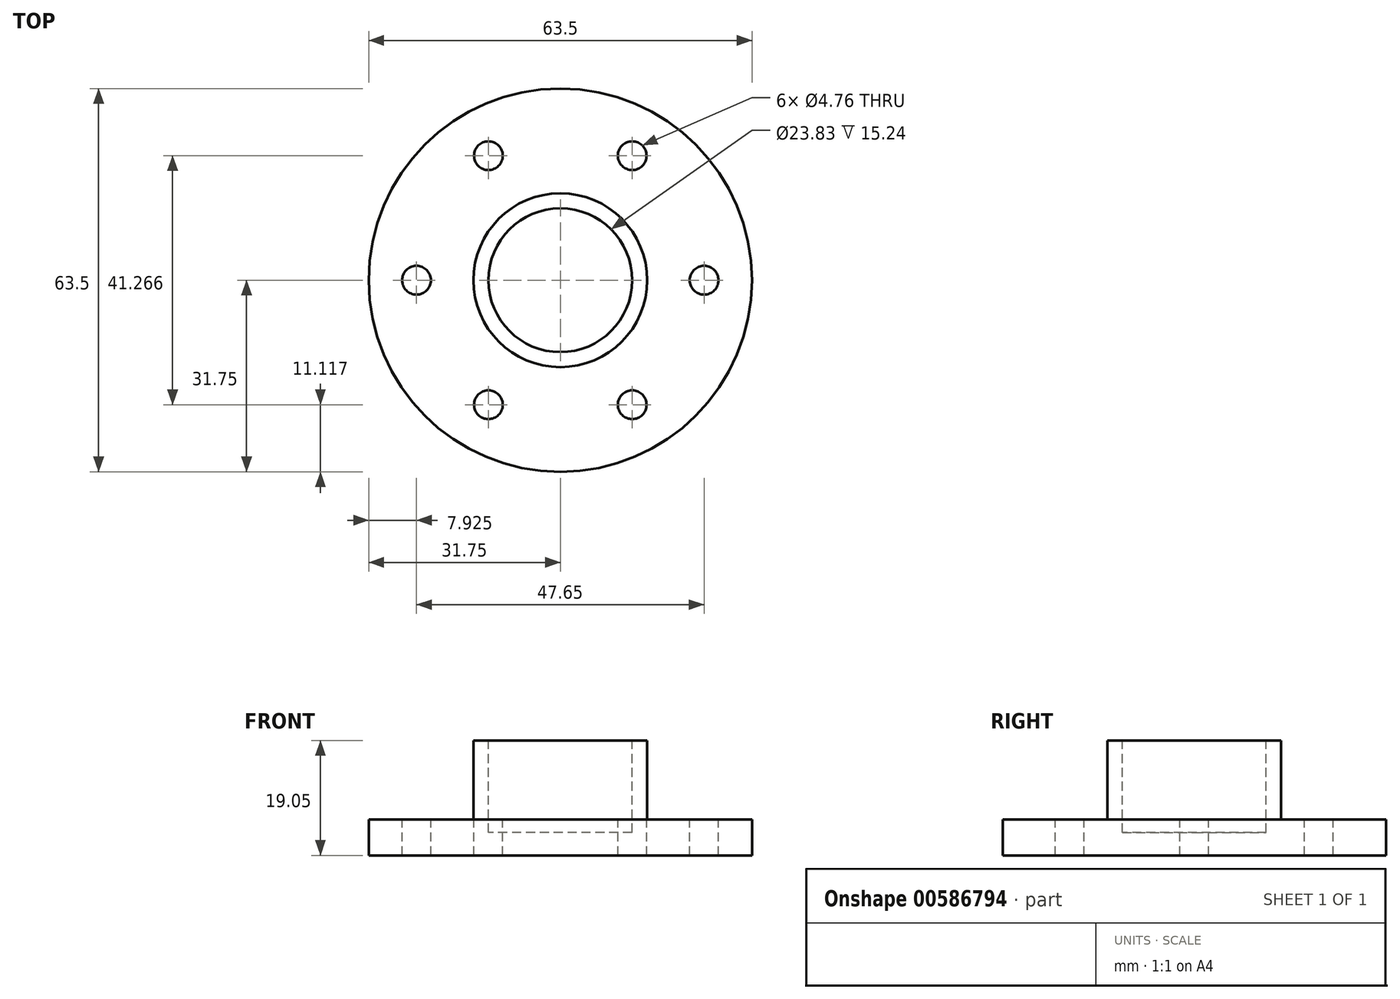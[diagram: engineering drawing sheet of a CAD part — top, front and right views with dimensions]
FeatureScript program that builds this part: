
annotation { "Feature Type Name" : "Feature", "Feature Type Description" : "" }
export const myFeature = defineFeature(function(context is Context, id is Id, definition is map)
    precondition{}
    {
        {
            var Q0;
            Q0=qCreatedBy(makeId("Top.planeOp"),FACE);
            var sketch = newSketch(context, id + "F0", { "sketchPlane" : qUnion([Q0])});
            skCircle(sketch, "E0", {"center": v(0, 0) * mm, "radius": 31.75 * mm});
            skSolve(sketch);
        }
        {
            var Q0;
            Q0=makeQuery(id+"F0.imprint","IMPRINT",FACE,{"disambiguationData":[TD([[makeQuery(id+"F0.imprint","IMPRINT",EDGE,{"derivedFrom":sQuery(id+"F0.wireOp",EDGE,"E0")}),1.0]])]});
            extrude(context, id + "F1", {"entities" : qUnion([Q0]), "oppositeDirection" : true, "depth" : 5.95 * mm, "offsetDistance" : 25.4 * mm});
        }
        {
            var Q0;
            Q0=makeQuery(id+"F1.opExtrude","CAP_FACE",FACE,{"disambiguationData":[OSD([sQuery(id+"F0.wireOp",EDGE,"E0")])],"isStart":true});
            var sketch = newSketch(context, id + "F2", { "sketchPlane" : qUnion([Q0])});
            skCircle(sketch, "E1", {"center": v(0, 0) * mm, "radius": 14.4 * mm});
            skSolve(sketch);
        }
        {
            var Q0;
            Q0=makeQuery(id+"F2.imprint","IMPRINT",FACE,{"disambiguationData":[TD([[makeQuery(id+"F2.imprint","IMPRINT",EDGE,{"derivedFrom":sQuery(id+"F2.wireOp",EDGE,"E1")}),1.0]])]});
            extrude(context, id + "F3", {"entities" : qUnion([Q0]), "operationType" : NewBodyOperationType.ADD, "depth" : 13.1 * mm, "offsetDistance" : 25.4 * mm});
        }
        {
            var Q0;
            Q0=makeQuery(id+"F3.opExtrude","CAP_FACE",FACE,{"disambiguationData":[OSD([sQuery(id+"F2.wireOp",EDGE,"E1")])],"isStart":false});
            var sketch = newSketch(context, id + "F4", { "sketchPlane" : qUnion([Q0])});
            skCircle(sketch, "E2", {"center": v(0, 0) * mm, "radius": 11.91 * mm});
            skSolve(sketch);
        }
        {
            var Q0;
            Q0=makeQuery(id+"F1.opExtrude","CAP_FACE",FACE,{"disambiguationData":[OSD([sQuery(id+"F0.wireOp",EDGE,"E0")])],"isStart":true});
            var sketch = newSketch(context, id + "F5", { "sketchPlane" : qUnion([Q0])});
            skCircle(sketch, "E3.cCircle", {"center": v(0, 0) * mm, "radius": 20.63 * mm, "construction": true});
            skLineSegment(sketch, "E3.0", {"start": v(-11.91, 20.63) * mm, "end": v(11.91, 20.63) * mm, "construction": true});
            skLineSegment(sketch, "E3.1", {"start": v(11.91, 20.63) * mm, "end": v(23.83, 0) * mm, "construction": true});
            skLineSegment(sketch, "E3.2", {"start": v(23.83, 0) * mm, "end": v(11.91, -20.63) * mm, "construction": true});
            skLineSegment(sketch, "E3.3", {"start": v(11.91, -20.63) * mm, "end": v(-11.91, -20.63) * mm, "construction": true});
            skLineSegment(sketch, "E3.4", {"start": v(-11.91, -20.63) * mm, "end": v(-23.83, 0) * mm, "construction": true});
            skLineSegment(sketch, "E3.5", {"start": v(-23.83, 0) * mm, "end": v(-11.91, 20.63) * mm, "construction": true});
            skPoint(sketch, "E3.0.midPoint", {"position": v(0, 20.63) * mm});
            skCircle(sketch, "E4", {"center": v(-23.83, 0) * mm, "radius": 2.38 * mm});
            skCircle(sketch, "E5", {"center": v(-11.91, 20.63) * mm, "radius": 2.38 * mm});
            skCircle(sketch, "E6", {"center": v(11.91, 20.63) * mm, "radius": 2.38 * mm});
            skCircle(sketch, "E7", {"center": v(23.83, 0) * mm, "radius": 2.38 * mm});
            skCircle(sketch, "E8", {"center": v(11.91, -20.63) * mm, "radius": 2.38 * mm});
            skCircle(sketch, "E9", {"center": v(-11.91, -20.63) * mm, "radius": 2.38 * mm});
            skSolve(sketch);
        }
        {
            var Q0;
            Q0 = qSketchRegion(id + "F5", true);
            extrude(context, id + "F6", {"entities" : qUnion([Q0]), "operationType" : NewBodyOperationType.REMOVE, "endBound" : BoundingType.THROUGH_ALL, "oppositeDirection" : true, "depth" : 25.4 * mm, "offsetDistance" : 25.4 * mm});
        }
        {
            var Q0;
            Q0=makeQuery(id+"F4.imprint","IMPRINT",FACE,{"disambiguationData":[TD([[makeQuery(id+"F4.imprint","IMPRINT",EDGE,{"derivedFrom":sQuery(id+"F4.wireOp",EDGE,"E2")}),1.0]])]});
            var Q1;
            Q1=sQuery(id+"F4.wireOp",EDGE,"E2");
            extrude(context, id + "F7", {"entities" : qUnion([Q0]), "operationType" : NewBodyOperationType.REMOVE, "surfaceEntities" : qUnion([Q1]), "oppositeDirection" : true, "depth" : 15.24 * mm, "offsetDistance" : 25.4 * mm});
        }
    });
